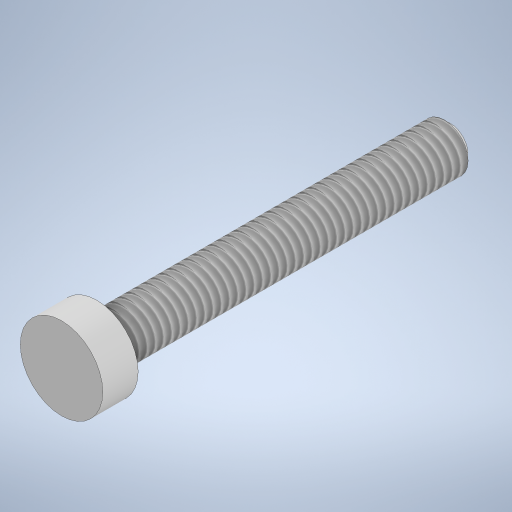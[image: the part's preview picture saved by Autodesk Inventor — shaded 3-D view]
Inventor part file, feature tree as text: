
AUTODESK INVENTOR PART (.ipt)
format: ipt  version: 2023 (Build 270158000, 158)  size: 273,920 bytes
history: native  units: mm
features: other x1, revolve x1, thread x1, chamfer x1, sketch x1
ambient origin geometry x8: Origin, YZ Plane, XZ Plane, XY Plane, X Axis, Y Axis, Z Axis, Center Point
bodies: Body1 (feature_tree)
feature tree (5):
  other  "Твердое тело1"
  revolve  "Вращение1"
  thread  "Резьба1"
  chamfer  "Фаска1"  Distance=3.5mm
  sketch  "Эскиз1"
